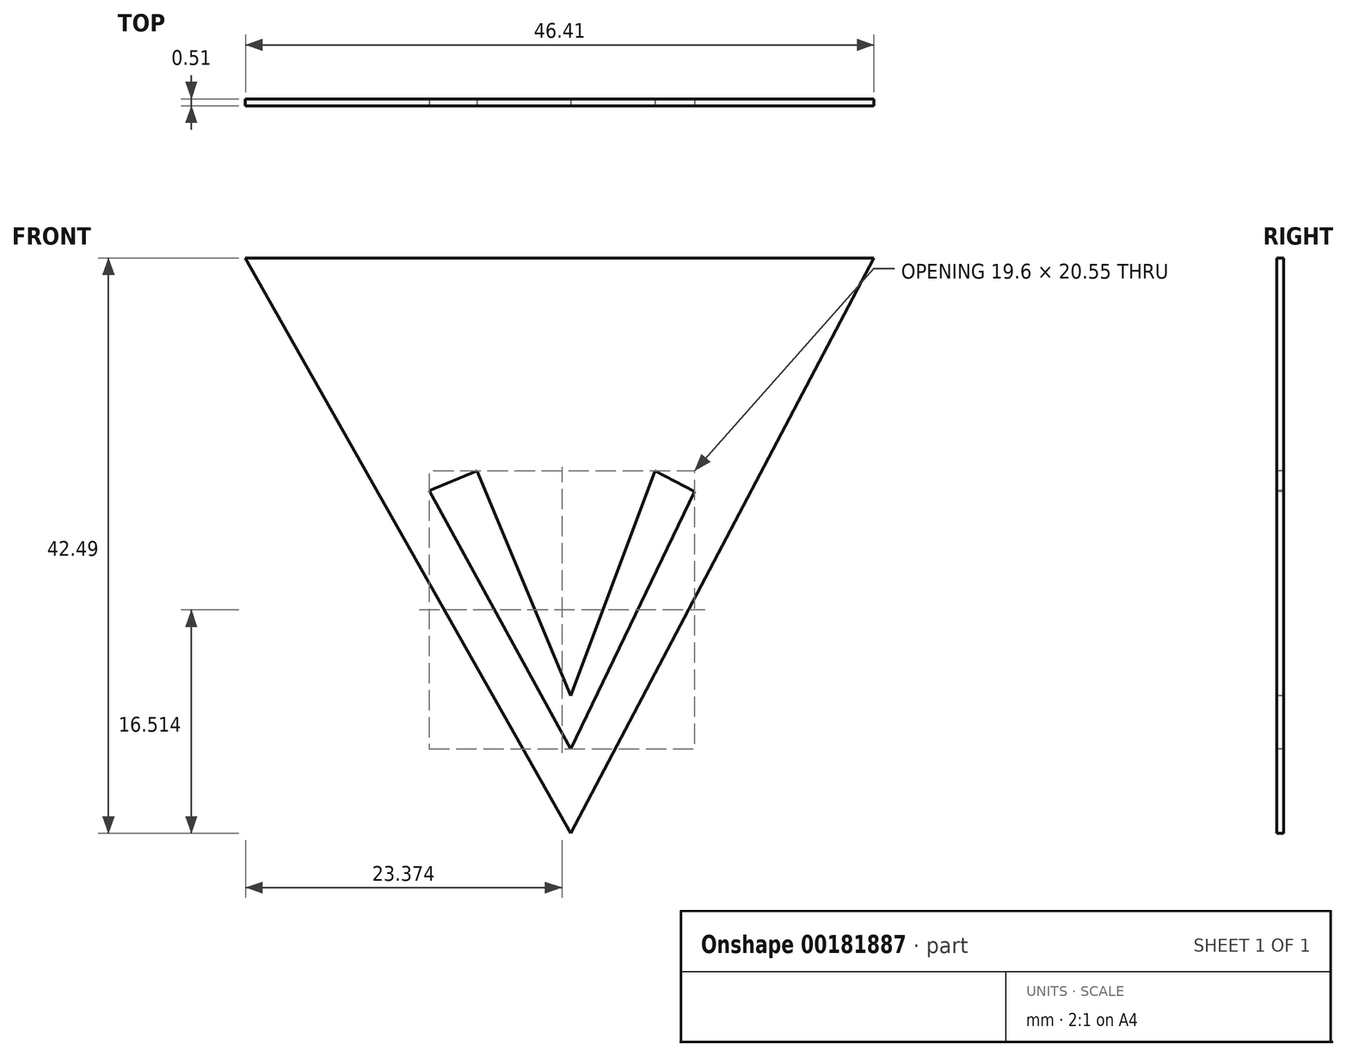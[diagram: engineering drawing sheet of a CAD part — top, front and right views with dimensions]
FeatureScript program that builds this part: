
annotation { "Feature Type Name" : "Feature", "Feature Type Description" : "" }
export const myFeature = defineFeature(function(context is Context, id is Id, definition is map)
    precondition{}
    {
        {
            var Q0;
            Q0=qCreatedBy(makeId("Front.planeOp"),FACE);
            var sketch = newSketch(context, id + "F0", { "sketchPlane" : qUnion([Q0])});
            skLineSegment(sketch, "E0", {"start": v(9.1, 15.59) * mm, "end": v(9.24, 15.82) * mm});
            skLineSegment(sketch, "E1", {"start": v(9, 15.59) * mm, "end": v(9.1, 15.59) * mm});
            skLineSegment(sketch, "E2", {"start": v(-24.01, 21.82) * mm, "end": v(22.4, 21.82) * mm});
            skLineSegment(sketch, "E3", {"start": v(22.4, 21.82) * mm, "end": v(0, -20.67) * mm});
            skLineSegment(sketch, "E4", {"start": v(-24.01, 21.82) * mm, "end": v(0, -20.67) * mm});
            skPoint(sketch, "E5.orphan", {"position": v(0, 0) * mm});
            skPoint(sketch, "E6.start.orphan", {"position": v(-9.47, 15.82) * mm});
            skPoint(sketch, "E7.end.orphan", {"position": v(0, -14.43) * mm});
            skLineSegment(sketch, "E8", {"start": v(0, -20.67) * mm, "end": v(0, -14.43) * mm});
            skLineSegment(sketch, "E9", {"start": v(-6.93, 6.12) * mm, "end": v(0, -10.5) * mm});
            skLineSegment(sketch, "E10", {"start": v(0, -10.5) * mm, "end": v(6.23, 6.12) * mm});
            skLineSegment(sketch, "E11", {"start": v(-6.93, 6.12) * mm, "end": v(-10.44, 4.66) * mm});
            skLineSegment(sketch, "E12", {"start": v(6.23, 6.12) * mm, "end": v(9.16, 4.57) * mm});
            skLineSegment(sketch, "E13", {"start": v(9.16, 4.57) * mm, "end": v(0, -14.43) * mm});
            skLineSegment(sketch, "E14", {"start": v(-10.44, 4.66) * mm, "end": v(0, -14.43) * mm});
            skSolve(sketch);
        }
        {
            var Q0;
            Q0=makeQuery(id+"F0.imprint","IMPRINT",FACE,{"disambiguationData":[TD([[makeQuery(id+"F0.imprint","IMPRINT",EDGE,{"derivedFrom":sQuery(id+"F0.wireOp",EDGE,"E2")}),-1.0]])]});
            extrude(context, id + "F1", {"entities" : qUnion([Q0]), "oppositeDirection" : true, "depth" : 0.5 * mm});
        }
    });
